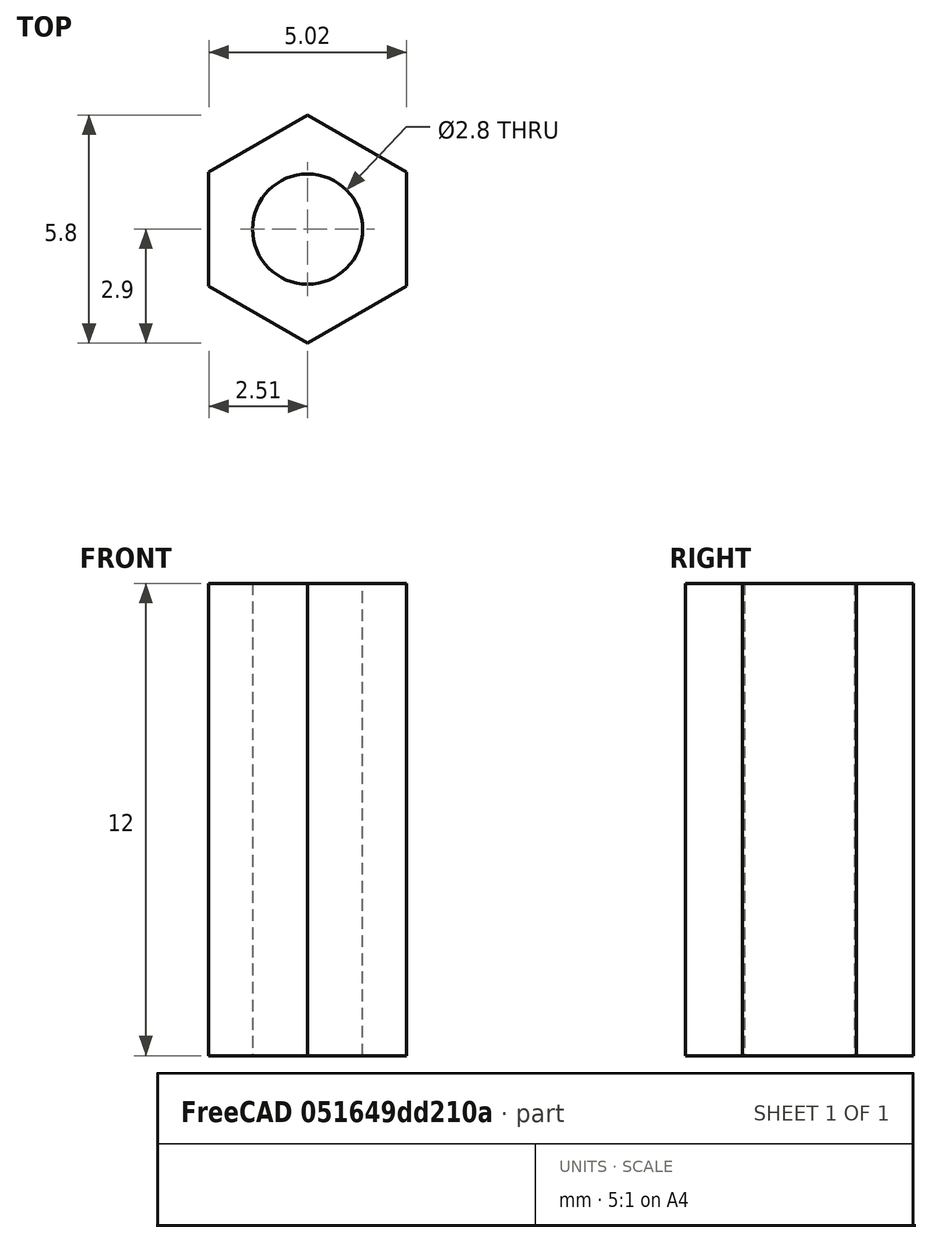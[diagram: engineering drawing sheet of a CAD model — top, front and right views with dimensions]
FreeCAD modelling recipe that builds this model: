
FCSTD DOCUMENT  (FreeCAD 0.18R16146 (Git))
Label: LCD_spacer
License: All rights reserved
LicenseURL: http://en.wikipedia.org/wiki/All_rights_reserved
objects: Sketcher::SketchObject×1, PartDesign::Pad×1, PartDesign::Body×1
note: 4 computed .brp shape members not serialized (recipe doc carries the construction recipe); baked Part::Feature solids carry a one-line shape summary decoded from their .brp

FEATURE [Sketcher::SketchObject] Sketch
  MapMode = 5
  Support = -> [XY_Plane]
  sketch-geometry (8):
    g0: LineSegment StartX=2.51147 StartY=1.45 StartZ=0 EndX=0 EndY=2.9 EndZ=0
    g1: LineSegment StartX=0 StartY=2.9 StartZ=0 EndX=-2.51147 EndY=1.45 EndZ=0
    g2: LineSegment StartX=-2.51147 StartY=1.45 StartZ=0 EndX=-2.51147 EndY=-1.45 EndZ=0
    g3: LineSegment StartX=-2.51147 StartY=-1.45 StartZ=0 EndX=-4e-16 EndY=-2.9 EndZ=0
    g4: LineSegment StartX=-4e-16 StartY=-2.9 StartZ=0 EndX=2.51147 EndY=-1.45 EndZ=0
    g5: LineSegment StartX=2.51147 StartY=-1.45 StartZ=0 EndX=2.51147 EndY=1.45 EndZ=0
    g6: Circle [constr] CenterX=0 CenterY=0 CenterZ=0 NormalX=0 NormalY=0 NormalZ=1 AngleXU=0 Radius=2.9
    g7: Circle CenterX=0 CenterY=0 CenterZ=0 NormalX=0 NormalY=0 NormalZ=1 AngleXU=0 Radius=1.4
  constraints (18):
    c: Coincident(g0,g1)
    c: Coincident(g1,g2)
    c: Coincident(g2,g3)
    c: Coincident(g3,g4)
    c: Coincident(g4,g5)
    c: Coincident(g5,g0)
    c: Equal(g0, g1-g5) x5
    c: PointOnObject(g0,g6)
    c: PointOnObject(g1,g6)
    c: PointOnObject(g2,g6)
    c: PointOnObject(g3,g6)
    c: PointOnObject(g4,g6)
    c: PointOnObject(g5,g6)
    c: Coincident(g6,g-1)
    c: Vertical(g5)
    c: Coincident(g7,g-1)
    c: Diameter(g7) = 2.8
    c: Diameter(g6) = 5.8
FEATURE [PartDesign::Pad] Pad
  Length = 12
  Length2 = 100
  Profile = -> Sketch
  Type = 0
FEATURE [PartDesign::Body] Body
  Group = -> [Sketch,Pad]
  Origin = -> Origin
  Tip = -> Pad
